# Revit family: Arper_Catifa53_chair_trestlefixed_upholstery_3144
name_source: partatom
category: Furniture
units: mm (PartAtom-declared; Revit-internal decimal feet)

## family parameters
Always vertical = Yes
Cut with Voids When Loaded = No
OmniClass Number = 23.40.20.00
OmniClass Title = General Furniture and Specialties
Room Calculation Point = No
Shared = No
Work Plane-Based = No

## types (1)
- Arper_Catifa53_chair_trestlefixed_upholstery_3144
    Default Elevation = 0 mm  [stored 0 ft]
    Description = Chair on fixed trestle base in polished or powder-coated aluminum 
mounted on self-braking castors (in the same color as the base). 
Polypropylene shell upholstered with fabric, leather, coated fabric or 
customer's own material, available in three stitching variants: striped, 
star-shaped or no stitching. In the striped variant, the stitching is the 
same color as the upholstery. In the star-shaped variant, the
stitching is available in white or black at the customer's choice. The 
upholstery is separable and replaceable, being applied without the 
use of glue.
    Manufacturer = ARPER s.p.a.
    Model = Catifa 53
    URL = http://www.arper.com

note: [stored X ft] marks values corroborated as IEEE doubles in the binary element streams (Revit-internal decimal feet)
